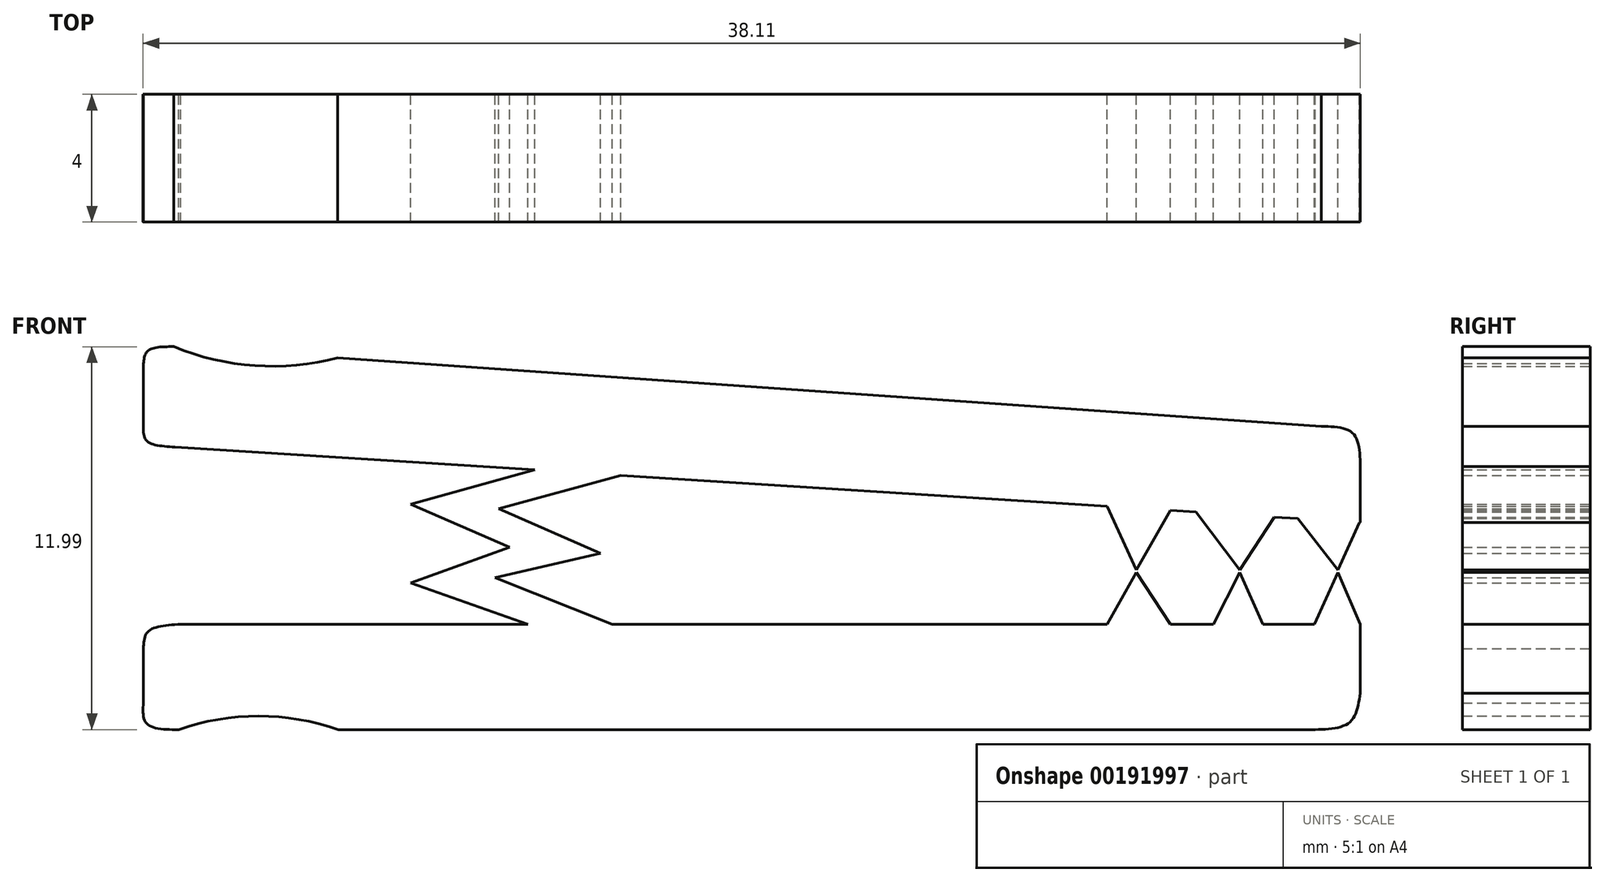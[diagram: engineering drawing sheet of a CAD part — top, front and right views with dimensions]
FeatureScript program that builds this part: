
annotation { "Feature Type Name" : "Feature", "Feature Type Description" : "" }
export const myFeature = defineFeature(function(context is Context, id is Id, definition is map)
    precondition{}
    {
        {
            var Q0;
            Q0=qCreatedBy(makeId("Front.planeOp"),FACE);
            var sketch = newSketch(context, id + "F0", { "sketchPlane" : qUnion([Q0])});
            skLineSegment(sketch, "E0", {"start": v(19.56, 0) * mm, "end": v(19.56, -2.16) * mm});
            skArc(sketch, "E1", {"start": v(-12.44, -3.3) * mm, "mid": v(-14.94, -2.88) * mm, "end": v(-17.44, -3.3) * mm});
            skLineSegment(sketch, "E2", {"start": v(18.12, 0) * mm, "end": v(18.86, 1.62) * mm});
            skLineSegment(sketch, "E3", {"start": v(18.86, 1.62) * mm, "end": v(19.56, 0) * mm});
            skLineSegment(sketch, "E4", {"start": v(16.5, 0) * mm, "end": v(15.8, 1.62) * mm});
            skLineSegment(sketch, "E5", {"start": v(15.8, 1.62) * mm, "end": v(14.96, 0) * mm});
            skLineSegment(sketch, "E6", {"start": v(18.86, 1.7) * mm, "end": v(19.54, 3.19) * mm});
            skLineSegment(sketch, "E7", {"start": v(18.86, 1.7) * mm, "end": v(17.6, 3.3) * mm});
            skLineSegment(sketch, "E8", {"start": v(15.8, 1.7) * mm, "end": v(16.87, 3.36) * mm});
            skLineSegment(sketch, "E9", {"start": v(15.8, 1.7) * mm, "end": v(14.42, 3.51) * mm});
            skLineSegment(sketch, "E10", {"start": v(19.56, 3.18) * mm, "end": v(-17.64, 5.55) * mm});
            skLineSegment(sketch, "E11", {"start": v(19.56, 3.18) * mm, "end": v(19.56, 5.21) * mm});
            skPoint(sketch, "E12.orphan", {"position": v(14.96, 2.8) * mm});
            skPoint(sketch, "E13.orphan", {"position": v(16.5, 2.8) * mm});
            skPoint(sketch, "E14.orphan", {"position": v(18, 2.8) * mm});
            skArc(sketch, "E15", {"start": v(-17.59, 8.7) * mm, "mid": v(-15.05, 8.1) * mm, "end": v(-12.46, 8.34) * mm});
            skLineSegment(sketch, "E16", {"start": v(-17.44, -3.3) * mm, "end": v(-17.44, -3.3) * mm});
            skLineSegment(sketch, "E17", {"start": v(-17.59, 8.7) * mm, "end": v(-17.6, 8.7) * mm});
            skLineSegment(sketch, "E18", {"start": v(-6.29, 4.83) * mm, "end": v(-10.18, 3.76) * mm});
            skLineSegment(sketch, "E19", {"start": v(-10.18, 3.76) * mm, "end": v(-7.08, 2.4) * mm});
            skLineSegment(sketch, "E20", {"start": v(-7.08, 2.4) * mm, "end": v(-10.18, 1.3) * mm});
            skLineSegment(sketch, "E21", {"start": v(-10.18, 1.3) * mm, "end": v(-6.29, -0.07) * mm});
            skLineSegment(sketch, "E22", {"start": v(-4.23, 2.21) * mm, "end": v(-7.53, 1.46) * mm});
            skLineSegment(sketch, "E23", {"start": v(-7.53, 1.46) * mm, "end": v(-3.87, 0) * mm});
            skLineSegment(sketch, "E24", {"start": v(-4.23, 2.21) * mm, "end": v(-7.42, 3.61) * mm});
            skLineSegment(sketch, "E25", {"start": v(-7.42, 3.61) * mm, "end": v(-3.59, 4.66) * mm});
            skLineSegment(sketch, "E26", {"start": v(-18.54, 6.22) * mm, "end": v(-18.54, 8.16) * mm});
            skFitSpline(sketch, "E27", {"points": [v(-18.54, 6.22) * mm, v(-18.44, 5.74) * mm, v(-17.56, 5.55) * mm], "startDerivative": vector(-0.03, -1.3) * mm, "endDerivative": vector(1.9, -0.11) * mm});
            skLineSegment(sketch, "E28", {"start": v(18.34, 6.2) * mm, "end": v(-12.46, 8.34) * mm});
            skFitSpline(sketch, "E29", {"points": [v(18.34, 6.2) * mm, v(19.33, 5.98) * mm, v(19.56, 4.94) * mm], "startDerivative": vector(2.38, -0.05) * mm, "endDerivative": vector(0.06, -2.45) * mm});
            skLineSegment(sketch, "E30", {"start": v(-18.54, -2.46) * mm, "end": v(-18.54, -0.76) * mm});
            skLineSegment(sketch, "E31", {"start": v(-17.37, 0) * mm, "end": v(19.56, 0) * mm});
            skFitSpline(sketch, "E32", {"points": [v(-18.54, -0.76) * mm, v(-18.39, -0.23) * mm, v(-17.37, 0) * mm], "startDerivative": vector(0.07, 1.45) * mm, "endDerivative": vector(2.16, 0.14) * mm});
            skFitSpline(sketch, "E33", {"points": [v(-18.54, -2.46) * mm, v(-18.43, -3.12) * mm, v(-17.44, -3.3) * mm], "startDerivative": vector(-0.1, -1.72) * mm, "endDerivative": vector(2.23, -0.02) * mm});
            skFitSpline(sketch, "E34", {"points": [v(-18.54, 8.16) * mm, v(-18.4, 8.56) * mm, v(-17.59, 8.7) * mm], "startDerivative": vector(0.11, 1.12) * mm, "endDerivative": vector(1.7, 0) * mm});
            skLineSegment(sketch, "E35", {"start": v(18.14, -3.3) * mm, "end": v(-12.44, -3.3) * mm});
            skFitSpline(sketch, "E36", {"points": [v(18.14, -3.3) * mm, v(19.24, -3.06) * mm, v(19.56, -2.16) * mm], "startDerivative": vector(2.48, 0.1) * mm, "endDerivative": vector(0.33, 2.22) * mm});
            skLineSegment(sketch, "E37", {"start": v(13.62, 3.56) * mm, "end": v(12.55, 1.7) * mm});
            skLineSegment(sketch, "E38", {"start": v(12.55, 1.7) * mm, "end": v(11.63, 3.69) * mm});
            skLineSegment(sketch, "E39", {"start": v(13.62, 0) * mm, "end": v(12.55, 1.62) * mm});
            skPoint(sketch, "E40.orphan", {"position": v(18, -0.26) * mm});
            skLineSegment(sketch, "E41", {"start": v(12.55, 1.62) * mm, "end": v(11.63, 0) * mm});
            skSolve(sketch);
        }
        {
            var Q0;
            Q0 = qSketchRegion(id + "F0", true);
            extrude(context, id + "F1", {"entities" : qUnion([Q0]), "depth" : 4 * mm});
        }
    });
